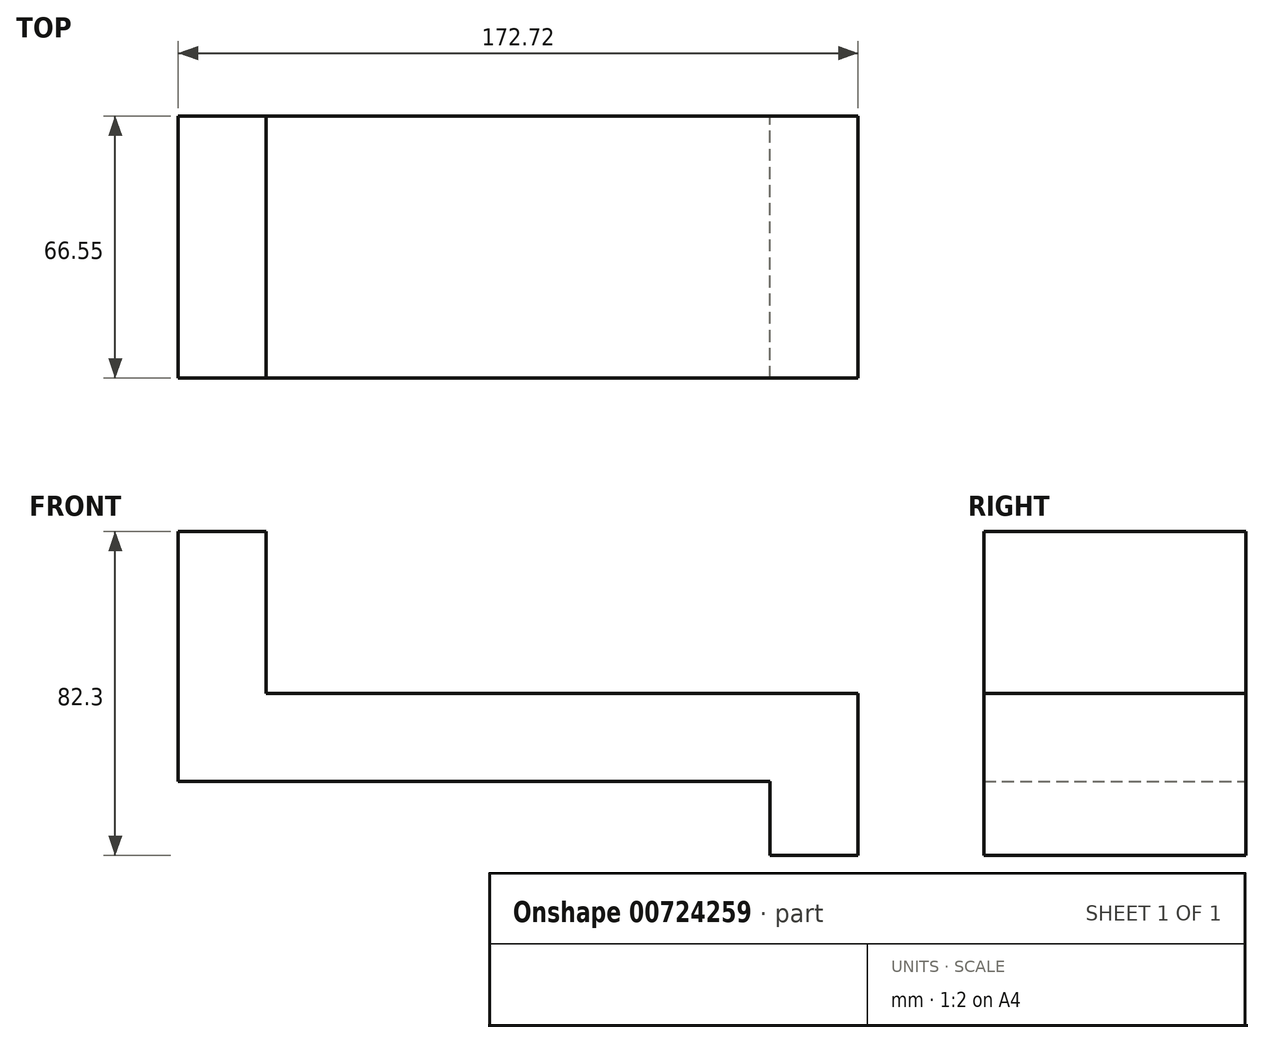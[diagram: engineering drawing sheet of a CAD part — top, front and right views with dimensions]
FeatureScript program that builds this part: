
annotation { "Feature Type Name" : "Feature", "Feature Type Description" : "" }
export const myFeature = defineFeature(function(context is Context, id is Id, definition is map)
    precondition{}
    {
        {
            var Q0;
            Q0=qCreatedBy(makeId("Front.planeOp"),FACE);
            var sketch = newSketch(context, id + "F0", { "sketchPlane" : qUnion([Q0])});
            skLineSegment(sketch, "E0", {"start": v(-76.17, 41.15) * mm, "end": v(-76.17, -22.35) * mm});
            skLineSegment(sketch, "E1", {"start": v(-76.17, -22.35) * mm, "end": v(74.2, -22.35) * mm});
            skLineSegment(sketch, "E2", {"start": v(-76.17, 41.15) * mm, "end": v(-53.82, 41.15) * mm});
            skLineSegment(sketch, "E3", {"start": v(-53.82, 41.15) * mm, "end": v(-53.82, 0) * mm});
            skLineSegment(sketch, "E4", {"start": v(-53.82, 0) * mm, "end": v(96.55, 0) * mm});
            skLineSegment(sketch, "E5", {"start": v(74.2, -22.35) * mm, "end": v(74.2, -41.15) * mm});
            skLineSegment(sketch, "E6", {"start": v(74.2, -41.15) * mm, "end": v(96.55, -41.15) * mm});
            skLineSegment(sketch, "E7", {"start": v(96.55, -41.15) * mm, "end": v(96.55, 0) * mm});
            skSolve(sketch);
        }
        {
            var Q0;
            Q0=makeQuery(id+"F0.imprint","IMPRINT",FACE,{"disambiguationData":[TD([[makeQuery(id+"F0.imprint","IMPRINT",EDGE,{"derivedFrom":sQuery(id+"F0.wireOp",EDGE,"E0")}),1.0]])]});
            extrude(context, id + "F1", {"entities" : qUnion([Q0]), "depth" : 66.55 * mm, "offsetDistance" : 25.4 * mm});
        }
    });
